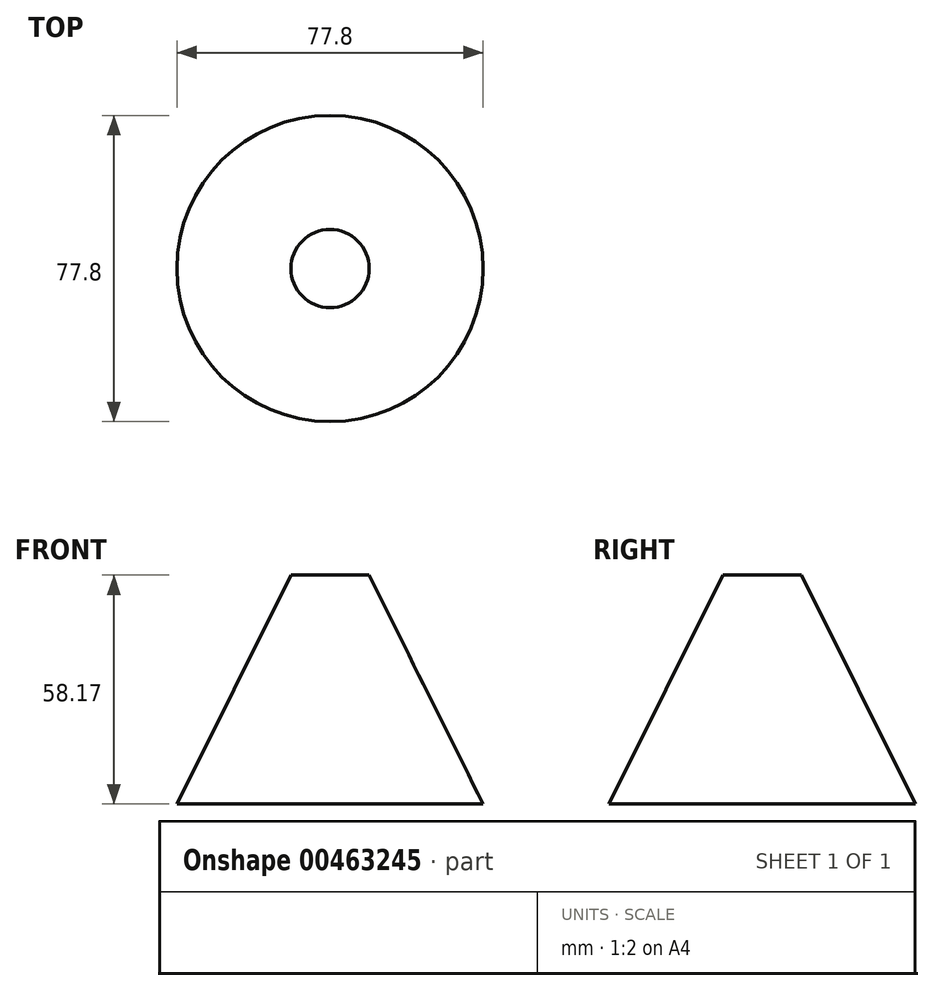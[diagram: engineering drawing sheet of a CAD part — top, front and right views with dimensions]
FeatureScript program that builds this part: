
annotation { "Feature Type Name" : "Feature", "Feature Type Description" : "" }
export const myFeature = defineFeature(function(context is Context, id is Id, definition is map)
    precondition{}
    {
        {
            var Q0;
            Q0=qCreatedBy(makeId("Top.planeOp"),FACE);
            var sketch = newSketch(context, id + "F0", { "sketchPlane" : qUnion([Q0])});
            skCircle(sketch, "E0", {"center": v(0, 0) * mm, "radius": 38.9 * mm});
            skSolve(sketch);
        }
        {
            var Q0;
            Q0=qCreatedBy(makeId("Top.planeOp"),FACE);
            cPlane(context, id + "F1", {"entities" : qUnion([Q0]), "cplaneType" : CPlaneType.OFFSET, "offset" : 58.17 * mm, "width" : 152.4 * mm, "height" : 152.4 * mm});
        }
        {
            var Q0;
            Q0=qCreatedBy(id+"F1.planeOp",FACE);
            var sketch = newSketch(context, id + "F2", { "sketchPlane" : qUnion([Q0])});
            skCircle(sketch, "E1", {"center": v(0, 0) * mm, "radius": 9.93 * mm});
            skSolve(sketch);
        }
        {
            var Q0;
            Q0=makeQuery(id+"F0.imprint","IMPRINT",FACE,{"disambiguationData":[TD([[makeQuery(id+"F0.imprint","IMPRINT",EDGE,{"derivedFrom":sQuery(id+"F0.wireOp",EDGE,"E0")}),1.0]])]});
            var Q1;
            Q1=makeQuery(id+"F2.imprint","IMPRINT",FACE,{"disambiguationData":[TD([[makeQuery(id+"F2.imprint","IMPRINT",EDGE,{"derivedFrom":sQuery(id+"F2.wireOp",EDGE,"E1")}),1.0]])]});
            loft(context, id + "F3", {"sheetProfilesArray" : [{ "sheetProfileEntities" : qUnion([Q0]) }, { "sheetProfileEntities" : qUnion([Q1]) }]});
        }
    });
